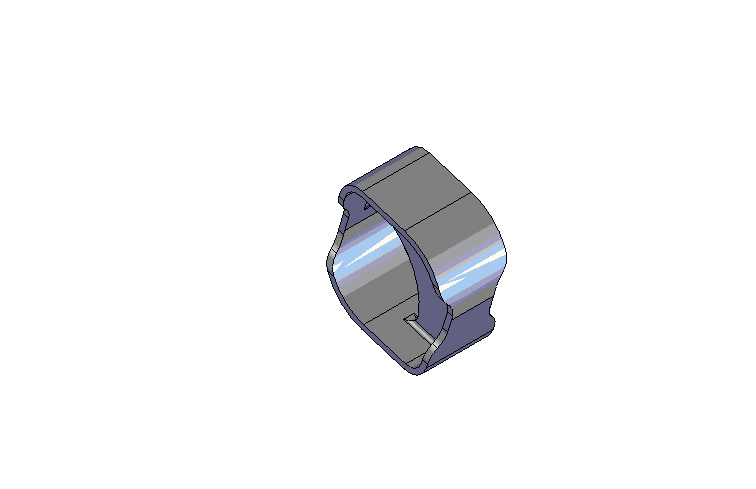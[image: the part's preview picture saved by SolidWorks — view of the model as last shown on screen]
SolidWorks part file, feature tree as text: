
SOLIDWORKS PART (.sldprt)
format: sldprt  version: not decoded by parser v0  size: 483,328 bytes
history: native  units: mm
features: plane x5, sketch x4, extrude x2, material x1, cut_extrude x1, fillet x1 (+10 scaffold rows collapsed)
feature tree (24):
  scaffold x10  (default folders/planes/origin — collapsed)
  material  "Matériau <non spécifié>"
  plane  "Plan de face"
  plane  "Plan de dessus"
  plane  "Plan de droite"
  sketch  "Esquisse1"  dims[c1.D1=625.0mm c1.D2=460.0mm c1.D3=545.0mm c1.D4=27.0mm c1.D5=500.0mm c1.D6=445.0mm c1.D7=670.0mm c2.D1=622.0mm c2.D2=670.0mm c2.D3=545.0mm c2.D4=460.0mm c2.D5=445.0mm c2.D6=495.0mm c2.D7=535.0mm c2.D8=27.0mm c2.D9=8.0mm c2.D10=155.0mm c2.D11=400.0mm c2.D12=~545.374305mm c3.D12=56.0deg]
  plane  "Plan6"
  plane  "Plan7"  Offset=287mm
  sketch  "Esquisse12"  dims[D3=10.0mm D4=30.0mm D1=65.0mm D2=65.0mm D6=255.0mm D7=16.0mm D5=3.0mm]
  extrude  "Extrusion2"  Depth=38mm
  sketch  "Esquisse16"  dims[c1.D1=22.0mm c1.D2=22.0mm c1.D3=5.0mm c1.D4=40.0mm c1.D5=5.0mm c2.D2=2.0mm c2.D5=41.0mm]
  extrude  "Extrusion3"  Depth=2mm
  sketch  "Esquisse13"  dims[D1=10.0mm D2=24.0mm D3=40.0mm]
  cut_extrude  "Enlèv. mat.-Extru.1"  [1 undecoded]
  fillet  "Congé1"  Radius=2mm
decode coverage: 7 of 8 modeling features carry decoded parameters
note: ~ marks probable driven/reference dimensions
note: 1 parameter value undecoded
note: suppression state not decoded; provenance and decode notes live in map.json
